# Revit family: UM362K-C Banco Ecosens
name_source: partatom
category: Mobiliario
units: mm (PartAtom-declared; Revit-internal decimal feet)

## family parameters
Compartido = No
Corte con vacíos al cargar = No
Número OmniClass = 23.40.20.00
Punto de cálculo de habitación = No
Se basa en plano de trabajo = No
Siempre vertical = Sí
Título OmniClass = General Furniture and Specialties

## types (1)
- UM362K-C Banco Ecosens
    Acabado Listones = Polímeros reciclados.
    Acabado bancada = Ferrus, proceso protector del hierro, que garantiza una óptima resistencia a la corrosión. Acabado imprimación epoxi y pintura poliéster en polvo.
    Accessibilidad = Sí
    Altura asiento = 440 mm  [stored 1.44357 ft]
    Altura total = 845 mm  [stored 2.77231 ft]
    Ancho = 725 mm  [stored 2.37861 ft]
    Comentarios de tipo = Pies de acero de 50x8 mm con tratamiento Ferrus. Perfiles de polímeros reciclados de sección 110x40x1800mm. Ecológico, proviene de producto reciclado y a la vez es reciclable. No requiere mantenimiento. No se astilla ni se agrieta, tampoco se pudre ni se reseca. Resistente a la humedad. Alta resistencia a las inclemencias. Resistente y duradero.
    Fabricante = BENITO
    Ficha tecnica = http://www.benito.com
    Instalación = Fijación al suelo mediante 4 tornillos d'expansión Ø10, no suministrados.
    Largo = 1800 mm  [stored 5.90551 ft]
    Material bancada = Acero
    Material listones = Rebnew
    Modelo = Banco Ecosens
    Referencia = UM362K-C
    URL = http://www.benito.com
    URL Producto = http://www.benito.com

note: [stored X ft] marks values corroborated as IEEE doubles in the binary element streams (Revit-internal decimal feet)

## geometry (parser evidence)
native form markers: Blend x4
no freeform markers — native parametric forms only
